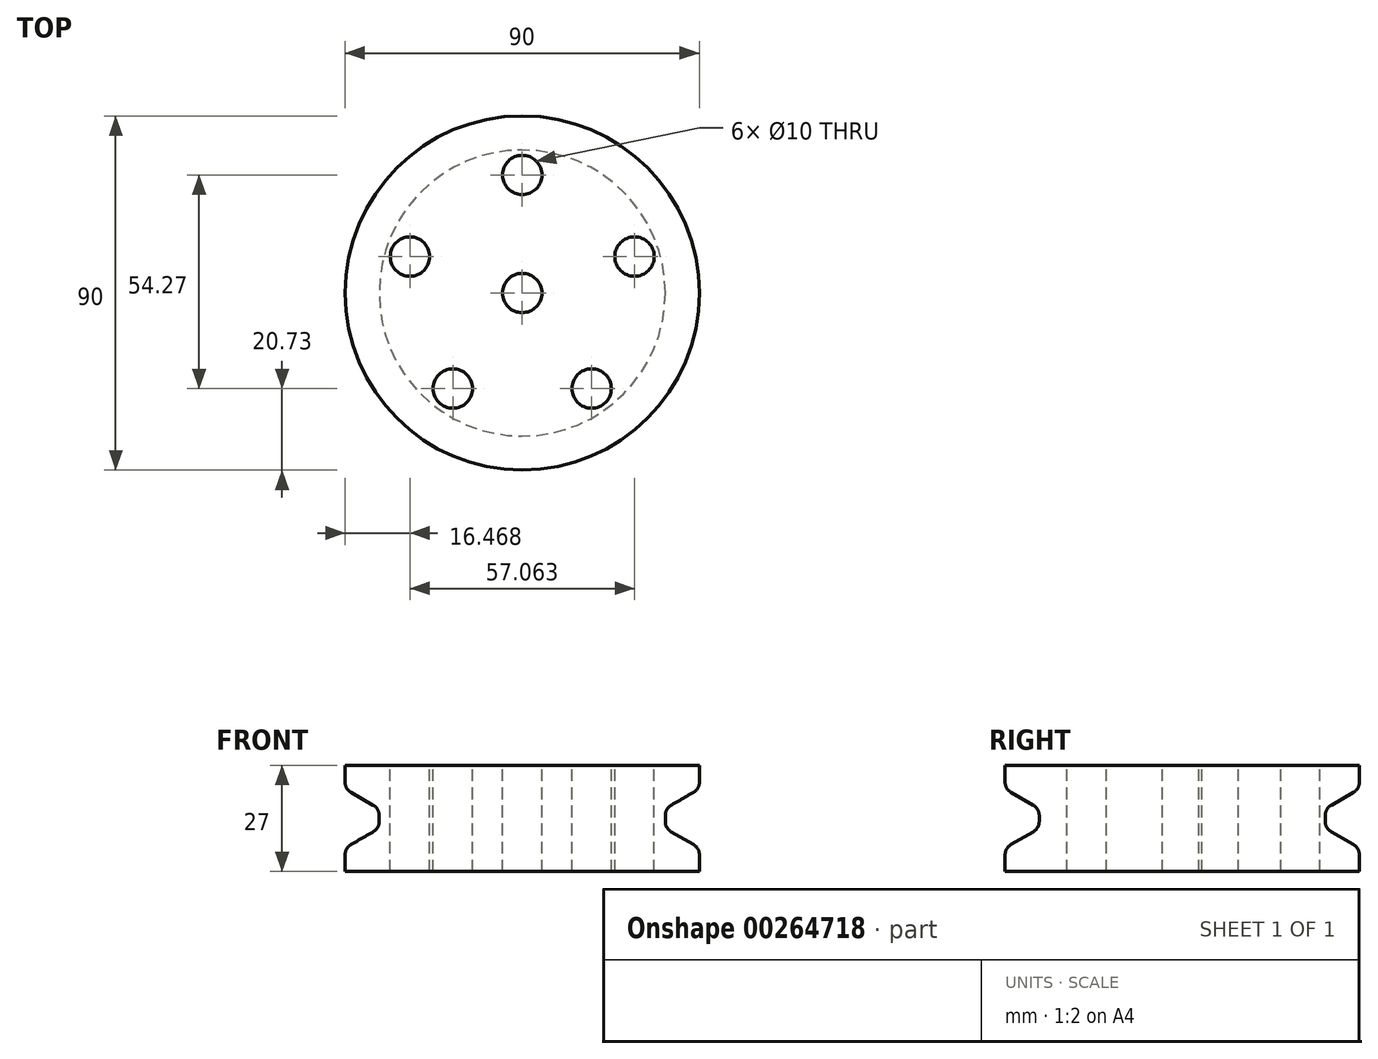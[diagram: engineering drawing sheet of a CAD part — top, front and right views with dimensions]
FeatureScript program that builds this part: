
annotation { "Feature Type Name" : "Feature", "Feature Type Description" : "" }
export const myFeature = defineFeature(function(context is Context, id is Id, definition is map)
    precondition{}
    {
        {
            var Q0;
            Q0=qCreatedBy(makeId("Right.planeOp"),FACE);
            var sketch = newSketch(context, id + "F0", { "sketchPlane" : qUnion([Q0])});
            skLineSegment(sketch, "E0", {"start": v(0, 32) * mm, "end": v(0, -31.46) * mm, "construction": true});
            skLineSegment(sketch, "E1", {"start": v(-5, -11) * mm, "end": v(-5, 16) * mm});
            skLineSegment(sketch, "E2", {"start": v(-5, 16) * mm, "end": v(-45, 16) * mm});
            skLineSegment(sketch, "E3", {"start": v(-45, 16) * mm, "end": v(-45, 10) * mm});
            skLineSegment(sketch, "E4", {"start": v(-45, 10) * mm, "end": v(-36.34, 5) * mm});
            skLineSegment(sketch, "E5", {"start": v(-36.34, 5) * mm, "end": v(-36.34, 0) * mm});
            skLineSegment(sketch, "E6", {"start": v(-36.34, 0) * mm, "end": v(-45, -5) * mm});
            skLineSegment(sketch, "E7", {"start": v(-45, -5) * mm, "end": v(-45, -11) * mm});
            skLineSegment(sketch, "E8", {"start": v(-45, -11) * mm, "end": v(-5, -11) * mm});
            skSolve(sketch);
        }
        {
            var Q0;
            Q0=makeQuery(id+"F0.imprint","IMPRINT",FACE,{"disambiguationData":[TD([[makeQuery(id+"F0.imprint","IMPRINT",EDGE,{"derivedFrom":sQuery(id+"F0.wireOp",EDGE,"E1")}),1.0]])]});
            var Q1;
            Q1=sQuery(id+"F0.wireOp",EDGE,"E0");
            revolve(context, id + "F1", {"entities" : qUnion([Q0]), "axis" : qUnion([Q1]), "revolveType" : RevolveType.FULL});
        }
        {
            var Q0;
            Q0=makeQuery(id+"F1.opRevolve","SWEPT_FACE",FACE,{"disambiguationData":[OSD([sQuery(id+"F0.wireOp",EDGE,"E2")])]});
            var sketch = newSketch(context, id + "F2", { "sketchPlane" : qUnion([Q0])});
            skCircle(sketch, "E9", {"center": v(0, 30) * mm, "radius": 5 * mm});
            skCircle(sketch, "E10.1.0", {"center": v(-28.53, 9.27) * mm, "radius": 5 * mm});
            skCircle(sketch, "E10.2.0", {"center": v(-17.63, -24.27) * mm, "radius": 5 * mm});
            skCircle(sketch, "E10.3.0", {"center": v(17.63, -24.27) * mm, "radius": 5 * mm});
            skCircle(sketch, "E10.4.0", {"center": v(28.53, 9.27) * mm, "radius": 5 * mm});
            skPoint(sketch, "E10.center", {"position": v(0, 0) * mm});
            skSolve(sketch);
        }
        {
            var Q0;
            Q0=makeQuery(id+"F2.imprint","IMPRINT",FACE,{"disambiguationData":[TD([[makeQuery(id+"F2.imprint","IMPRINT",EDGE,{"derivedFrom":sQuery(id+"F2.wireOp",EDGE,"E9")}),1.0]])]});
            var Q1;
            Q1=makeQuery(id+"F2.imprint","IMPRINT",FACE,{"disambiguationData":[TD([[makeQuery(id+"F2.imprint","IMPRINT",EDGE,{"derivedFrom":sQuery(id+"F2.wireOp",EDGE,"E10.1.0")}),1.0]])]});
            var Q2;
            Q2=makeQuery(id+"F2.imprint","IMPRINT",FACE,{"disambiguationData":[TD([[makeQuery(id+"F2.imprint","IMPRINT",EDGE,{"derivedFrom":sQuery(id+"F2.wireOp",EDGE,"E10.2.0")}),1.0]])]});
            var Q3;
            Q3=makeQuery(id+"F2.imprint","IMPRINT",FACE,{"disambiguationData":[TD([[makeQuery(id+"F2.imprint","IMPRINT",EDGE,{"derivedFrom":sQuery(id+"F2.wireOp",EDGE,"E10.3.0")}),1.0]])]});
            var Q4;
            Q4=makeQuery(id+"F2.imprint","IMPRINT",FACE,{"disambiguationData":[TD([[makeQuery(id+"F2.imprint","IMPRINT",EDGE,{"derivedFrom":sQuery(id+"F2.wireOp",EDGE,"E10.4.0")}),1.0]])]});
            extrude(context, id + "F3", {"entities" : qUnion([Q0, Q1, Q2, Q3, Q4]), "operationType" : NewBodyOperationType.REMOVE, "endBound" : BoundingType.UP_TO_NEXT, "oppositeDirection" : true, "depth" : 25 * mm});
        }
        {
            var Q0;
            Q0=makeQuery(id+"F1.opRevolve","SWEPT_EDGE",EDGE,{"disambiguationData":[OSD([sQuery(id+"F0.wireOp",EDGE,"E5"),sQuery(id+"F0.wireOp",EDGE,"E6")])]});
            var Q1;
            Q1=makeQuery(id+"F1.opRevolve","SWEPT_EDGE",EDGE,{"disambiguationData":[OSD([sQuery(id+"F0.wireOp",EDGE,"E4"),sQuery(id+"F0.wireOp",EDGE,"E5")])]});
            var Q2;
            Q2=makeQuery(id+"F1.opRevolve","SWEPT_EDGE",EDGE,{"disambiguationData":[OSD([sQuery(id+"F0.wireOp",EDGE,"E6"),sQuery(id+"F0.wireOp",EDGE,"E7")])]});
            var Q3;
            Q3=makeQuery(id+"F1.opRevolve","SWEPT_EDGE",EDGE,{"disambiguationData":[OSD([sQuery(id+"F0.wireOp",EDGE,"E3"),sQuery(id+"F0.wireOp",EDGE,"E4")])]});
            fillet(context, id + "F4", {"entities" : qUnion([Q0, Q1, Q2, Q3]), "radius" : 3 * mm, "tangentPropagation" : true, "allowEdgeOverflow" : false});
        }
    });
